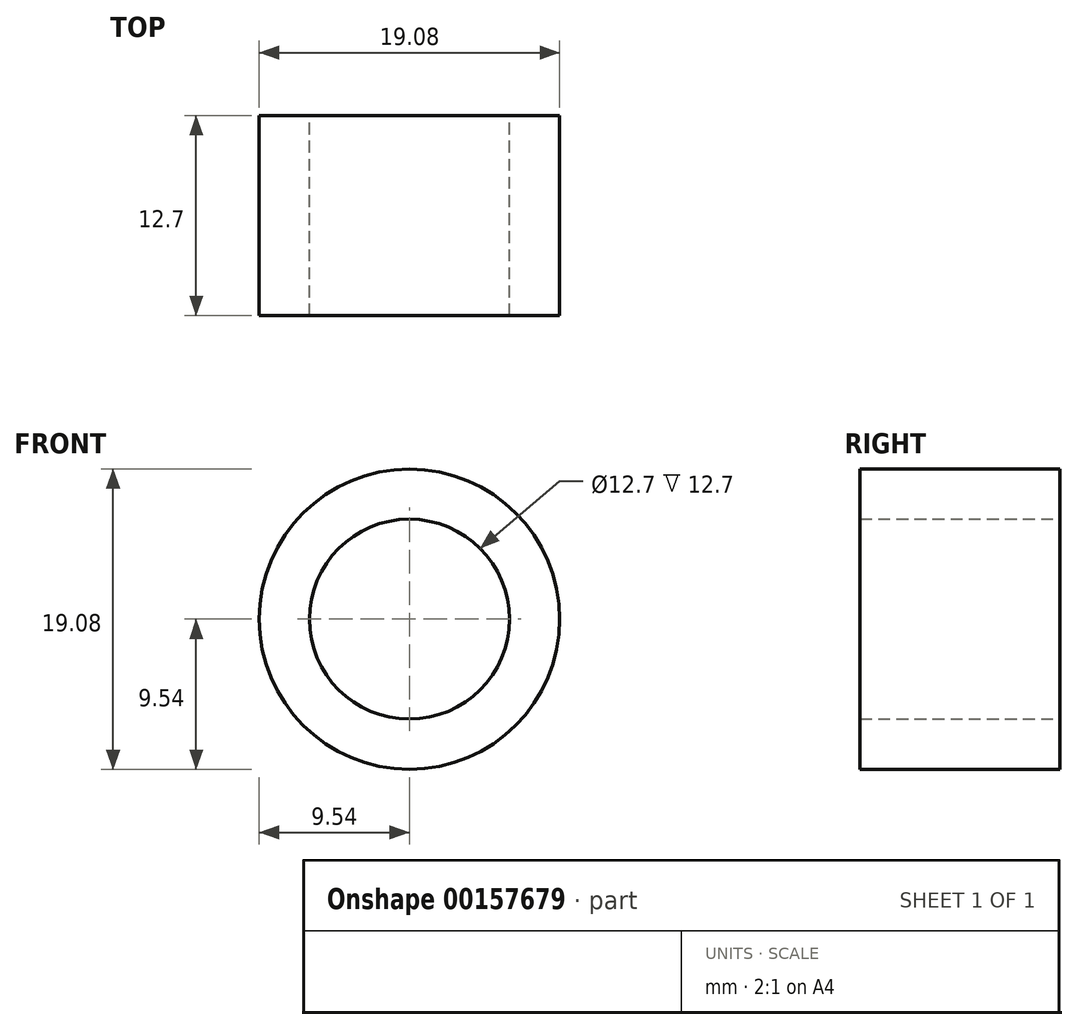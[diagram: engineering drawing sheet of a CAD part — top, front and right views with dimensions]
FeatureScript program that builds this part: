
annotation { "Feature Type Name" : "Feature", "Feature Type Description" : "" }
export const myFeature = defineFeature(function(context is Context, id is Id, definition is map)
    precondition{}
    {
        {
            var Q0;
            Q0=qCreatedBy(makeId("Front.planeOp"),FACE);
            var sketch = newSketch(context, id + "F0", { "sketchPlane" : qUnion([Q0])});
            skCircle(sketch, "E0", {"center": v(0, 0) * mm, "radius": 6.35 * mm});
            skCircle(sketch, "E1", {"center": v(0, 0) * mm, "radius": 9.54 * mm});
            skSolve(sketch);
        }
        {
            var Q0;
            Q0=makeQuery(id+"F0.imprint","IMPRINT",FACE,{"disambiguationData":[TD([[makeQuery(id+"F0.imprint","IMPRINT",EDGE,{"derivedFrom":sQuery(id+"F0.wireOp",EDGE,"E0")}),-1.0]])]});
            extrude(context, id + "F1", {"entities" : qUnion([Q0]), "endBound" : BoundingType.SYMMETRIC, "depth" : 12.7 * mm});
        }
    });
